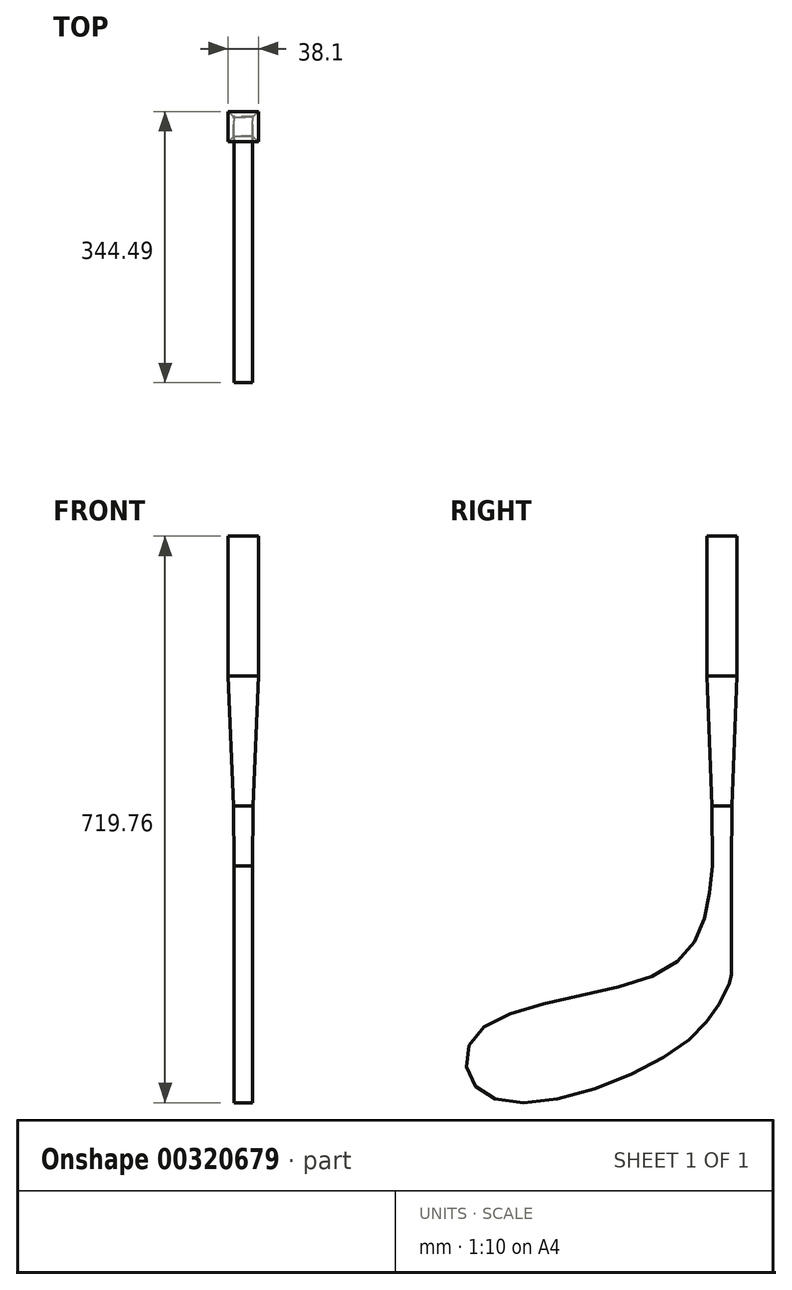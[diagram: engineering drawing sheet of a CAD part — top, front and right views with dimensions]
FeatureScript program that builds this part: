
annotation { "Feature Type Name" : "Feature", "Feature Type Description" : "" }
export const myFeature = defineFeature(function(context is Context, id is Id, definition is map)
    precondition{}
    {
        {
            var Q0;
            Q0=qCreatedBy(makeId("Top.planeOp"),FACE);
            var sketch = newSketch(context, id + "F0", { "sketchPlane" : qUnion([Q0])});
            skLineSegment(sketch, "E0.bottom", {"start": v(19.05, -19.05) * mm, "end": v(-19.05, -19.05) * mm});
            skLineSegment(sketch, "E0.top", {"start": v(19.05, 19.05) * mm, "end": v(-19.05, 19.05) * mm});
            skLineSegment(sketch, "E0.left", {"start": v(19.05, -19.05) * mm, "end": v(19.05, 19.05) * mm});
            skLineSegment(sketch, "E0.right", {"start": v(-19.05, -19.05) * mm, "end": v(-19.05, 19.05) * mm});
            skPoint(sketch, "E0.middle", {"position": v(0, 0) * mm});
            skSolve(sketch);
        }
        {
            var Q0;
            Q0 = qSketchRegion(id + "F0", true);
            extrude(context, id + "F1", {"entities" : qUnion([Q0]), "endBound" : BoundingType.SYMMETRIC, "oppositeDirection" : true, "depth" : 177.8 * mm});
        }
        {
            var Q0;
            Q0=qCreatedBy(makeId("Top.planeOp"),FACE);
            cPlane(context, id + "F2", {"entities" : qUnion([Q0]), "cplaneType" : CPlaneType.OFFSET, "offset" : 254 * mm, "oppositeDirection" : true, "width" : 152.4 * mm, "height" : 152.4 * mm});
        }
        {
            var Q0;
            Q0=qCreatedBy(id+"F2.planeOp",FACE);
            var sketch = newSketch(context, id + "F3", { "sketchPlane" : qUnion([Q0])});
            skLineSegment(sketch, "E1.bottom", {"start": v(12.7, -12.7) * mm, "end": v(-12.7, -12.7) * mm});
            skLineSegment(sketch, "E1.top", {"start": v(12.7, 12.7) * mm, "end": v(-12.7, 12.7) * mm});
            skLineSegment(sketch, "E1.left", {"start": v(12.7, -12.7) * mm, "end": v(12.7, 12.7) * mm});
            skLineSegment(sketch, "E1.right", {"start": v(-12.7, -12.7) * mm, "end": v(-12.7, 12.7) * mm});
            skPoint(sketch, "E1.middle", {"position": v(0, 0) * mm});
            skSolve(sketch);
        }
        {
            var Q1;
            Q1=makeQuery(id+"F1.opExtrude","CAP_FACE",FACE,{"disambiguationData":[OSD([sQuery(id+"F0.wireOp",EDGE,"E0.bottom"),sQuery(id+"F0.wireOp",EDGE,"E0.top"),sQuery(id+"F0.wireOp",EDGE,"E0.left"),sQuery(id+"F0.wireOp",EDGE,"E0.right")])],"isStart":false});
            var Q2;
            Q2=makeQuery(id+"F3.imprint","IMPRINT",FACE,{"disambiguationData":[TD([[makeQuery(id+"F3.imprint","IMPRINT",EDGE,{"derivedFrom":sQuery(id+"F3.wireOp",EDGE,"E1.bottom")}),-1.0]])]});
            loft(context, id + "F4", {"operationType" : NewBodyOperationType.ADD, "sheetProfilesArray" : [{ "sheetProfileEntities" : qUnion([Q1]) }, { "sheetProfileEntities" : qUnion([Q2]) }]});
        }
        {
            var Q0;
            Q0=qCreatedBy(id+"F2.planeOp",FACE);
            cPlane(context, id + "F5", {"entities" : qUnion([Q0]), "cplaneType" : CPlaneType.OFFSET, "offset" : 76.2 * mm, "oppositeDirection" : true, "width" : 152.4 * mm, "height" : 152.4 * mm});
        }
        {
            var Q0;
            Q0=qCreatedBy(id+"F5.planeOp",FACE);
            var sketch = newSketch(context, id + "F6", { "sketchPlane" : qUnion([Q0])});
            skLineSegment(sketch, "E2.bottom", {"start": v(12.07, -12.07) * mm, "end": v(-12.07, -12.07) * mm});
            skLineSegment(sketch, "E2.top", {"start": v(12.07, 12.07) * mm, "end": v(-12.07, 12.06) * mm});
            skLineSegment(sketch, "E2.left", {"start": v(12.06, -12.07) * mm, "end": v(12.07, 12.07) * mm});
            skLineSegment(sketch, "E2.right", {"start": v(-12.07, -12.07) * mm, "end": v(-12.07, 12.06) * mm});
            skPoint(sketch, "E2.middle", {"position": v(0, 0) * mm});
            skSolve(sketch);
        }
        {
            var Q1;
            Q1=makeQuery(id+"F4.opLoft","CAP_FACE",FACE,{"disambiguationData":[OSD([makeQuery(id+"F3.imprint","IMPRINT",FACE,{"disambiguationData":[TD([[makeQuery(id+"F3.imprint","IMPRINT",EDGE,{"derivedFrom":sQuery(id+"F3.wireOp",EDGE,"E1.bottom")}),-1.0]])]})])],"isStart":true});
            var Q2;
            Q2=makeQuery(id+"F6.imprint","IMPRINT",FACE,{"disambiguationData":[TD([[makeQuery(id+"F6.imprint","IMPRINT",EDGE,{"derivedFrom":sQuery(id+"F6.wireOp",EDGE,"E2.bottom")}),-1.0]])]});
            loft(context, id + "F7", {"operationType" : NewBodyOperationType.ADD, "sheetProfilesArray" : [{ "sheetProfileEntities" : qUnion([Q1]) }, { "sheetProfileEntities" : qUnion([Q2]) }]});
        }
        {
            var Q0;
            Q0=qCreatedBy(id+"F5.planeOp",FACE);
            cPlane(context, id + "F8", {"entities" : qUnion([Q0]), "cplaneType" : CPlaneType.OFFSET, "offset" : 25.4 * mm, "oppositeDirection" : true, "width" : 152.4 * mm, "height" : 152.4 * mm});
        }
        {
            var Q0;
            Q0=makeQuery(id+"F7.opLoft","CAP_FACE",FACE,{"disambiguationData":[OSD([makeQuery(id+"F6.imprint","IMPRINT",FACE,{"disambiguationData":[TD([[makeQuery(id+"F6.imprint","IMPRINT",EDGE,{"derivedFrom":sQuery(id+"F6.wireOp",EDGE,"E2.bottom")}),-1.0]])]})])],"isStart":true});
            var sketch = newSketch(context, id + "F9", { "sketchPlane" : qUnion([Q0])});
            skLineSegment(sketch, "E3", {"start": v(0, 0) * mm, "end": v(0, 12.07) * mm});
            skLineSegment(sketch, "E4", {"start": v(0, 12.07) * mm, "end": v(0, -12.06) * mm});
            skSolve(sketch);
        }
        {
            var Q0;
            Q0=qCreatedBy(id+"F8.planeOp",FACE);
            var Q1;
            Q1=sQuery(id+"F9.wireOp",EDGE,"E4");
            cPlane(context, id + "F10", {"entities" : qUnion([Q0, Q1]), "cplaneType" : CPlaneType.LINE_ANGLE, "offset" : 25.4 * mm, "angle" : 90 * degree, "width" : 152.4 * mm, "height" : 152.4 * mm});
        }
        {
            var Q0;
            Q0=qCreatedBy(id+"F10.planeOp",FACE);
            var sketch = newSketch(context, id + "F11", { "sketchPlane" : qUnion([Q0])});
            skLineSegment(sketch, "E5", {"start": v(12.14, -330.2) * mm, "end": v(-12, -330.2) * mm});
            skLineSegment(sketch, "E6", {"start": v(-12, -330.2) * mm, "end": v(-12, -472.95) * mm});
            skFitSpline(sketch, "E7", {"points": [v(12.14, -330.2) * mm, v(68.25, -459.7) * mm, v(310.94, -541.93) * mm, v(297.98, -622.23) * mm, v(55.94, -561.42) * mm, v(-12, -472.95) * mm], "startDerivative": vector(77.73, -805.48) * mm, "endDerivative": vector(-235.46, 529.4) * mm});
            skSolve(sketch);
        }
        {
            var Q0;
            Q0=makeQuery(id+"F11.imprint","IMPRINT",FACE,{"disambiguationData":[TD([[makeQuery(id+"F11.imprint","IMPRINT",EDGE,{"derivedFrom":sQuery(id+"F11.wireOp",EDGE,"E5")}),1.0]])]});
            extrude(context, id + "F12", {"entities" : qUnion([Q0]), "operationType" : NewBodyOperationType.ADD, "endBound" : BoundingType.SYMMETRIC, "depth" : 24.13 * mm});
        }
        {
            var Q0;
            Q0=makeQuery(id+"F12.opExtrude","SWEPT_EDGE",EDGE,{"disambiguationData":[OSD([sQuery(id+"F11.wireOp",EDGE,"E6"),sQuery(id+"F11.wireOp",EDGE,"E7")])]});
            fillet(context, id + "F13", {"entities" : qUnion([Q0]), "radius" : 50.8 * mm, "tangentPropagation" : true, "allowEdgeOverflow" : false});
        }
    });
